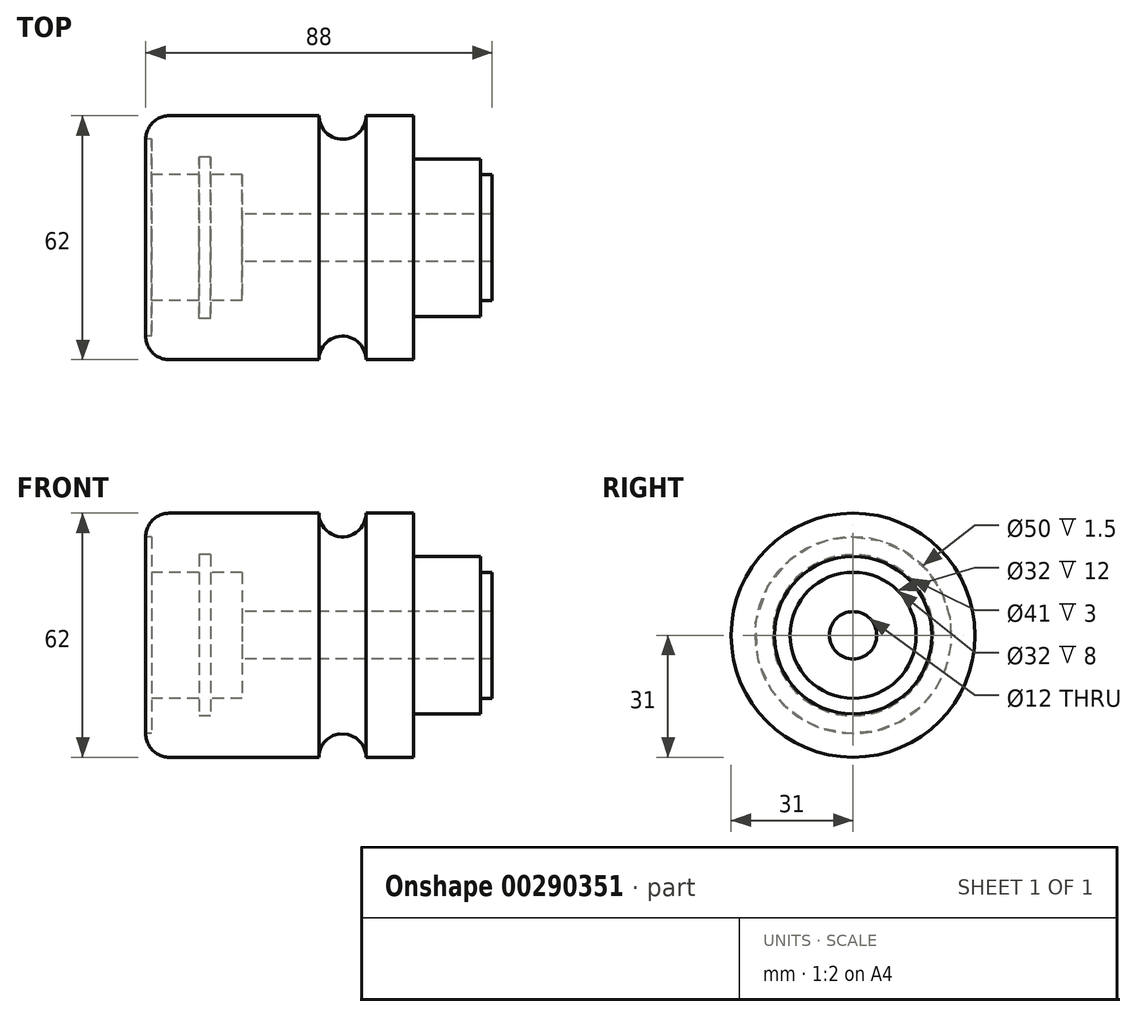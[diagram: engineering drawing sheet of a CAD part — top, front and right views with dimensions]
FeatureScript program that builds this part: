
annotation { "Feature Type Name" : "Feature", "Feature Type Description" : "" }
export const myFeature = defineFeature(function(context is Context, id is Id, definition is map)
    precondition{}
    {
        {
            var Q0;
            Q0=qCreatedBy(makeId("Front.planeOp"),FACE);
            var sketch = newSketch(context, id + "F0", { "sketchPlane" : qUnion([Q0])});
            skLineSegment(sketch, "E0", {"start": v(0, 0) * mm, "end": v(88, 0) * mm});
            skLineSegment(sketch, "E1", {"start": v(88, 0) * mm, "end": v(88, 16) * mm});
            skLineSegment(sketch, "E2", {"start": v(88, 16) * mm, "end": v(85, 16) * mm});
            skLineSegment(sketch, "E3", {"start": v(85, 16) * mm, "end": v(85, 20) * mm});
            skLineSegment(sketch, "E4", {"start": v(85, 20) * mm, "end": v(68, 20) * mm});
            skLineSegment(sketch, "E5", {"start": v(68, 20) * mm, "end": v(68, 31) * mm});
            skLineSegment(sketch, "E6", {"start": v(68, 31) * mm, "end": v(56, 31) * mm});
            skLineSegment(sketch, "E7", {"start": v(0, 25) * mm, "end": v(0, 0) * mm});
            skArc(sketch, "E8", {"start": v(44, 31) * mm, "mid": v(50, 25) * mm, "end": v(56, 31) * mm});
            skLineSegment(sketch, "E9", {"start": v(44, 31) * mm, "end": v(6, 31) * mm});
            skArc(sketch, "E10", {"start": v(6, 31) * mm, "mid": v(1.76, 29.24) * mm, "end": v(0, 25) * mm});
            skSolve(sketch);
        }
        {
            var Q0;
            Q0=makeQuery(id+"F0.imprint","IMPRINT",FACE,{"disambiguationData":[TD([[makeQuery(id+"F0.imprint","IMPRINT",EDGE,{"derivedFrom":sQuery(id+"F0.wireOp",EDGE,"E0")}),1.0]])]});
            var Q1;
            Q1=sQuery(id+"F0.wireOp",EDGE,"E0");
            revolve(context, id + "F1", {"entities" : qUnion([Q0]), "axis" : qUnion([Q1]), "revolveType" : RevolveType.FULL});
        }
        {
            var Q0;
            Q0=makeQuery(id+"F1.opRevolve","SWEPT_FACE",FACE,{"disambiguationData":[OSD([sQuery(id+"F0.wireOp",EDGE,"E7")])]});
            var sketch = newSketch(context, id + "F2", { "sketchPlane" : qUnion([Q0])});
            skCircle(sketch, "E11", {"center": v(0, 0) * mm, "radius": 25 * mm});
            skSolve(sketch);
        }
        {
            var Q0;
            Q0 = qSketchRegion(id + "F2", true);
            extrude(context, id + "F3", {"entities" : qUnion([Q0]), "operationType" : NewBodyOperationType.REMOVE, "oppositeDirection" : true, "depth" : 1.5 * mm});
        }
        {
            var Q0;
            Q0=makeQuery(id+"F3.boolean.opBoolean","COPY",FACE,{"derivedFrom":makeQuery(id+"F3.opExtrude","CAP_FACE",FACE,{"disambiguationData":[OSD([sQuery(id+"F2.wireOp",EDGE,"E11")])],"isStart":false})});
            var sketch = newSketch(context, id + "F4", { "sketchPlane" : qUnion([Q0])});
            skCircle(sketch, "E12", {"center": v(0, 0) * mm, "radius": 16 * mm});
            skSolve(sketch);
        }
        {
            var Q0;
            Q0 = qSketchRegion(id + "F4", true);
            extrude(context, id + "F5", {"entities" : qUnion([Q0]), "operationType" : NewBodyOperationType.REMOVE, "oppositeDirection" : true, "depth" : 12 * mm});
        }
        {
            var Q0;
            Q0=makeQuery(id+"F5.boolean.opBoolean","COPY",FACE,{"derivedFrom":makeQuery(id+"F5.opExtrude","CAP_FACE",FACE,{"disambiguationData":[OSD([sQuery(id+"F4.wireOp",EDGE,"E12")])],"isStart":false})});
            var sketch = newSketch(context, id + "F6", { "sketchPlane" : qUnion([Q0])});
            skCircle(sketch, "E13", {"center": v(0, 0) * mm, "radius": 20.5 * mm});
            skSolve(sketch);
        }
        {
            var Q0;
            Q0 = qSketchRegion(id + "F6", true);
            extrude(context, id + "F7", {"entities" : qUnion([Q0]), "operationType" : NewBodyOperationType.REMOVE, "oppositeDirection" : true, "depth" : 3 * mm});
        }
        {
            var Q0;
            Q0=makeQuery(id+"F7.boolean.opBoolean","COPY",FACE,{"derivedFrom":makeQuery(id+"F7.opExtrude","CAP_FACE",FACE,{"disambiguationData":[OSD([sQuery(id+"F6.wireOp",EDGE,"E13")])],"isStart":false})});
            var sketch = newSketch(context, id + "F8", { "sketchPlane" : qUnion([Q0])});
            skCircle(sketch, "E14", {"center": v(0, 0) * mm, "radius": 16 * mm});
            skSolve(sketch);
        }
        {
            var Q0;
            Q0 = qSketchRegion(id + "F8", true);
            extrude(context, id + "F9", {"entities" : qUnion([Q0]), "operationType" : NewBodyOperationType.REMOVE, "oppositeDirection" : true, "depth" : 8 * mm});
        }
        {
            var Q0;
            Q0=makeQuery(id+"F9.boolean.opBoolean","COPY",FACE,{"derivedFrom":makeQuery(id+"F9.opExtrude","CAP_FACE",FACE,{"disambiguationData":[OSD([sQuery(id+"F8.wireOp",EDGE,"E14")])],"isStart":false})});
            var sketch = newSketch(context, id + "F10", { "sketchPlane" : qUnion([Q0])});
            skCircle(sketch, "E15", {"center": v(0, 0) * mm, "radius": 6 * mm});
            skSolve(sketch);
        }
        {
            var Q0;
            Q0 = qSketchRegion(id + "F10", true);
            extrude(context, id + "F11", {"entities" : qUnion([Q0]), "operationType" : NewBodyOperationType.REMOVE, "endBound" : BoundingType.THROUGH_ALL, "oppositeDirection" : true, "depth" : 25 * mm});
        }
    });
